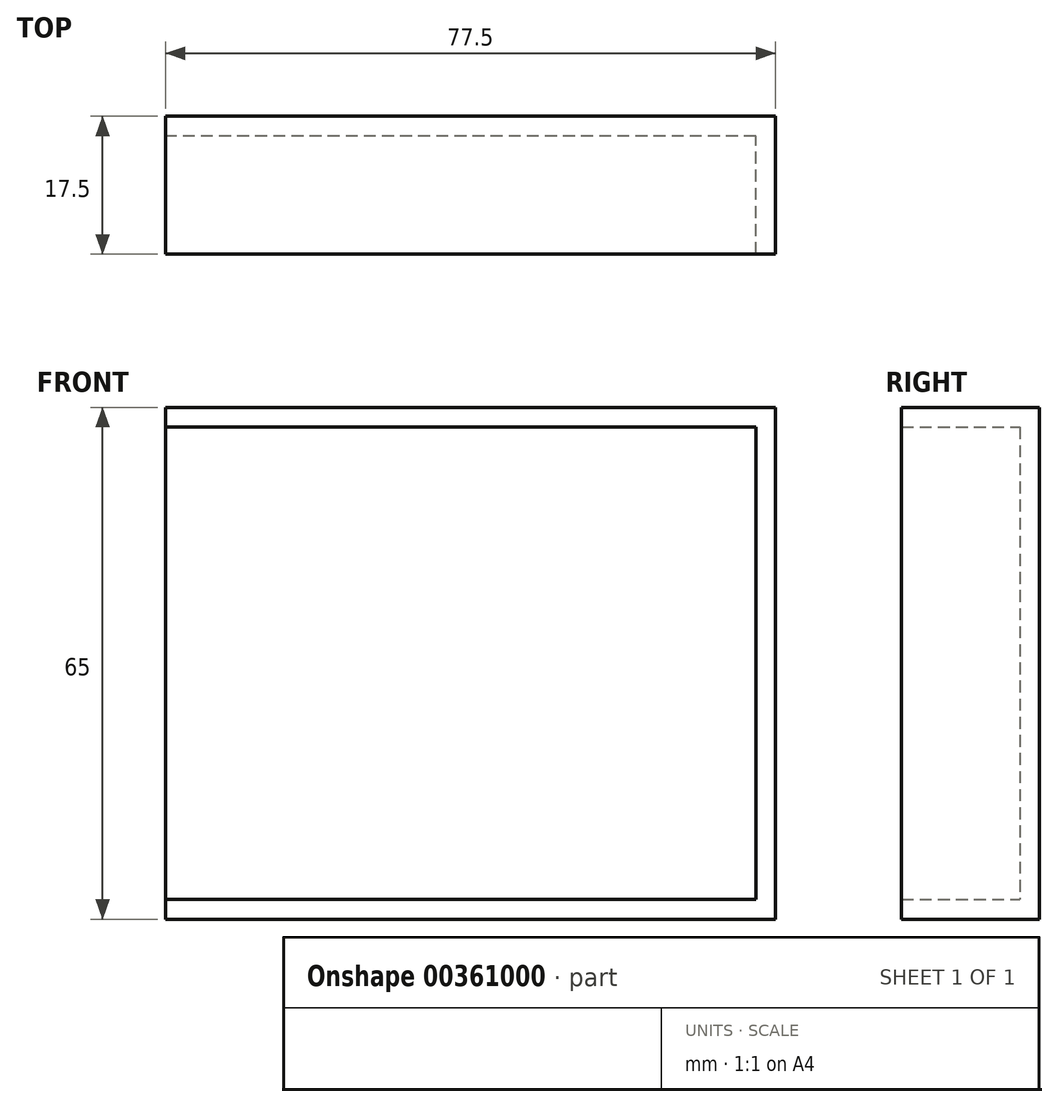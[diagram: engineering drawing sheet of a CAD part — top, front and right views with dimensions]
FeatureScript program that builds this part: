
annotation { "Feature Type Name" : "Feature", "Feature Type Description" : "" }
export const myFeature = defineFeature(function(context is Context, id is Id, definition is map)
    precondition{}
    {
        {
            var Q0;
            Q0=qCreatedBy(makeId("Front.planeOp"),FACE);
            var sketch = newSketch(context, id + "F0", { "sketchPlane" : qUnion([Q0])});
            skLineSegment(sketch, "E0.bottom", {"start": v(37.5, 30) * mm, "end": v(-37.5, 30) * mm});
            skLineSegment(sketch, "E0.top", {"start": v(37.5, -30) * mm, "end": v(-37.5, -30) * mm});
            skLineSegment(sketch, "E0.left", {"start": v(37.5, 30) * mm, "end": v(37.5, -30) * mm});
            skLineSegment(sketch, "E0.right", {"start": v(-37.5, 30) * mm, "end": v(-37.5, -30) * mm});
            skPoint(sketch, "E0.middle", {"position": v(0, 0) * mm});
            skSolve(sketch);
        }
        {
            var Q0;
            Q0 = qSketchRegion(id + "F0", true);
            extrude(context, id + "F1", {"entities" : qUnion([Q0]), "depth" : 15 * mm});
        }
        {
            var Q0;
            Q0=makeQuery(id+"F1.opExtrude","CAP_FACE",FACE,{"disambiguationData":[OSD([sQuery(id+"F0.wireOp",EDGE,"E0.bottom"),sQuery(id+"F0.wireOp",EDGE,"E0.top"),sQuery(id+"F0.wireOp",EDGE,"E0.left"),sQuery(id+"F0.wireOp",EDGE,"E0.right")])],"isStart":false});
            var Q1;
            Q1=makeQuery(id+"F1.opExtrude","SWEPT_FACE",FACE,{"disambiguationData":[OSD([sQuery(id+"F0.wireOp",EDGE,"E0.right")])]});
            shell(context, id + "F2", {"entities" : qUnion([Q0, Q1]), "thickness" : 2.5 * mm, "oppositeDirection" : true});
        }
    });
